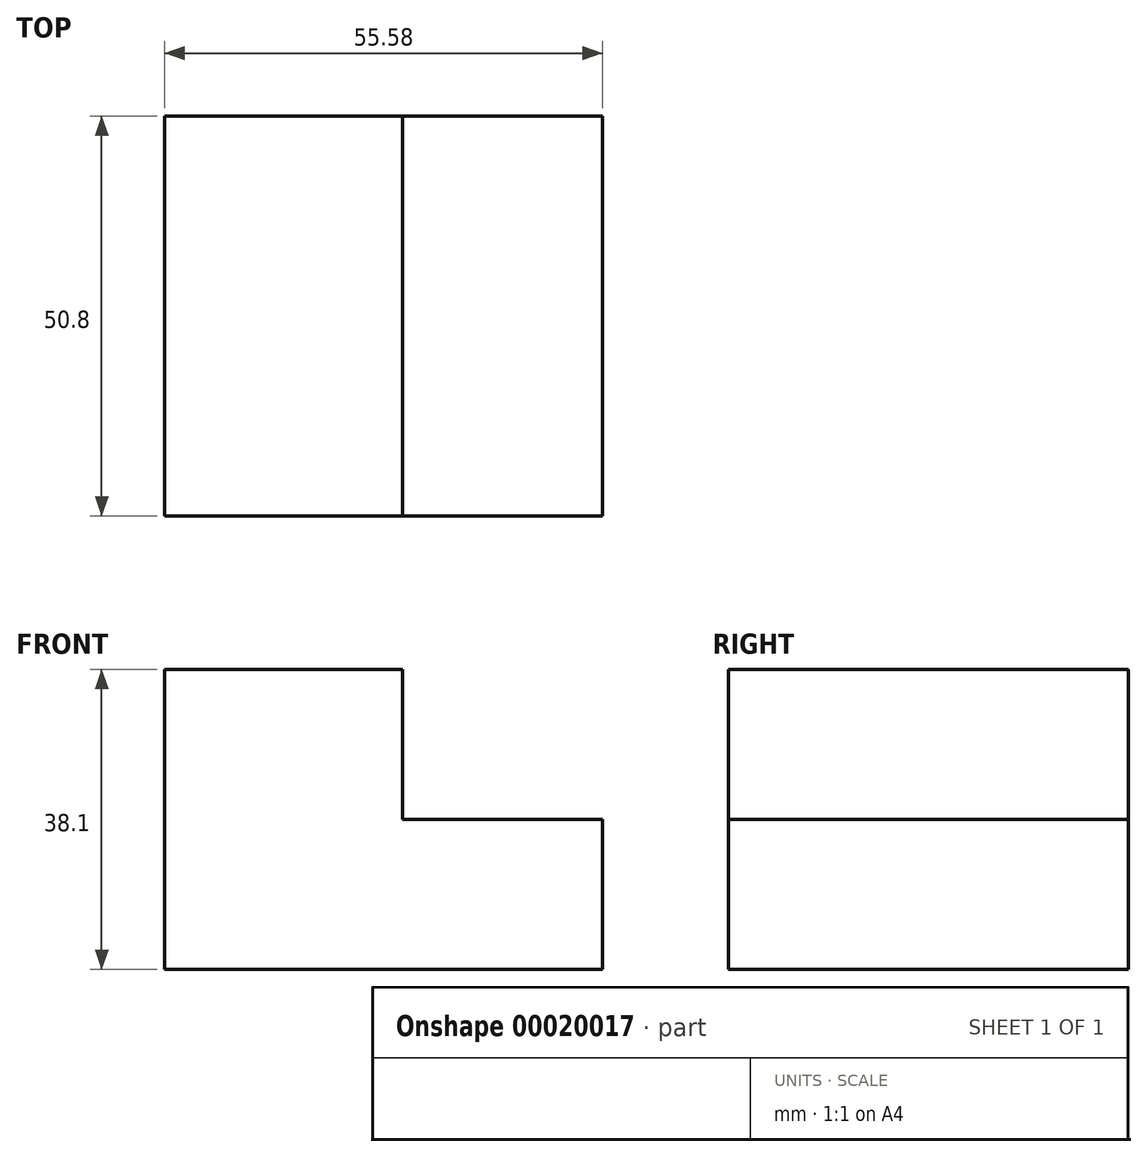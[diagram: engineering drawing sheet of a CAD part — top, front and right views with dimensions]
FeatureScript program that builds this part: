
annotation { "Feature Type Name" : "Feature", "Feature Type Description" : "" }
export const myFeature = defineFeature(function(context is Context, id is Id, definition is map)
    precondition{}
    {
        {
            var Q0;
            Q0=qCreatedBy(makeId("Front.planeOp"),FACE);
            var sketch = newSketch(context, id + "F0", { "sketchPlane" : qUnion([Q0])});
            skLineSegment(sketch, "E0.rect.bottom", {"start": v(-27.79, 19.05) * mm, "end": v(2.39, 19.05) * mm});
            skLineSegment(sketch, "E0.rect.top", {"start": v(-27.79, -19.05) * mm, "end": v(27.79, -19.05) * mm});
            skLineSegment(sketch, "E0.rect.left", {"start": v(-27.79, 19.05) * mm, "end": v(-27.79, -19.05) * mm});
            skLineSegment(sketch, "E0.rect.right", {"start": v(27.79, 0) * mm, "end": v(27.79, -19.05) * mm});
            skPoint(sketch, "E0.rect.middle", {"position": v(0, 0) * mm});
            skLineSegment(sketch, "E1.top", {"start": v(27.79, 0) * mm, "end": v(2.39, 0) * mm});
            skLineSegment(sketch, "E1.right", {"start": v(2.39, 19.05) * mm, "end": v(2.39, 0) * mm});
            skPoint(sketch, "E1.bottom.start.orphan", {"position": v(27.79, 19.05) * mm});
            skSolve(sketch);
        }
        {
            var Q0;
            Q0=makeQuery(id+"F0.imprint","IMPRINT",FACE,{"disambiguationData":[TD([[makeQuery(id+"F0.imprint","IMPRINT",EDGE,{"derivedFrom":sQuery(id+"F0.wireOp",EDGE,"E0.rect.bottom")}),-1.0]])]});
            extrude(context, id + "F1", {"entities" : qUnion([Q0]), "depth" : 50.8 * mm});
        }
    });
